# Revit family: Trim-Modern_Dots-Waterworks-Universal-Thermostatic_Valveq
name_source: partatom
category: Plumbing Fixtures
revit_build: Autodesk Revit MEP 2014 (Build: 20140709_2115(x64)
units: mm (PartAtom-declared; Revit-internal decimal feet)

## types (1)
- NOT A TYPE - Load Type Catalog
    Assembly Code = C1030200
    CW Connection = No
    Constraint = 1
    ControlM = 1
    Default Elevation = 3' - 0"
    Description = Universal Two Way Diverter Valve Trim for Thermostatic in Antique Brass
    Finish = Metal - Waterworks - Chrome
    HW Connection = No
    Height = 0' - 3 3/4"
    Keynote = 22 40 00
    Length = 0' - 0 3/16"
    Manufacturer = Waterworks
    Model = UN2TM1
    Model SKU = 05-22928-42878
    Product Documentation Link = http://assets.waterworks.com
    Product Name = Universal Two Way Diverter Valve Trim for Thermostatic in Antique Brass
    Product Page URL = http://www.waterworks.com
    Three Way Diverter = No
    Two Way Diverter = Yes
    URL = http://www.waterworks.com
    Vent Connection = No
    Version = 2014 - v1.0a
    Warranty = http://www.waterworks.com
    Waste Connection = No
    Width = 0' - 3 3/4"

## geometry (parser evidence)
native form markers: Sweep x3
no freeform markers — native parametric forms only
